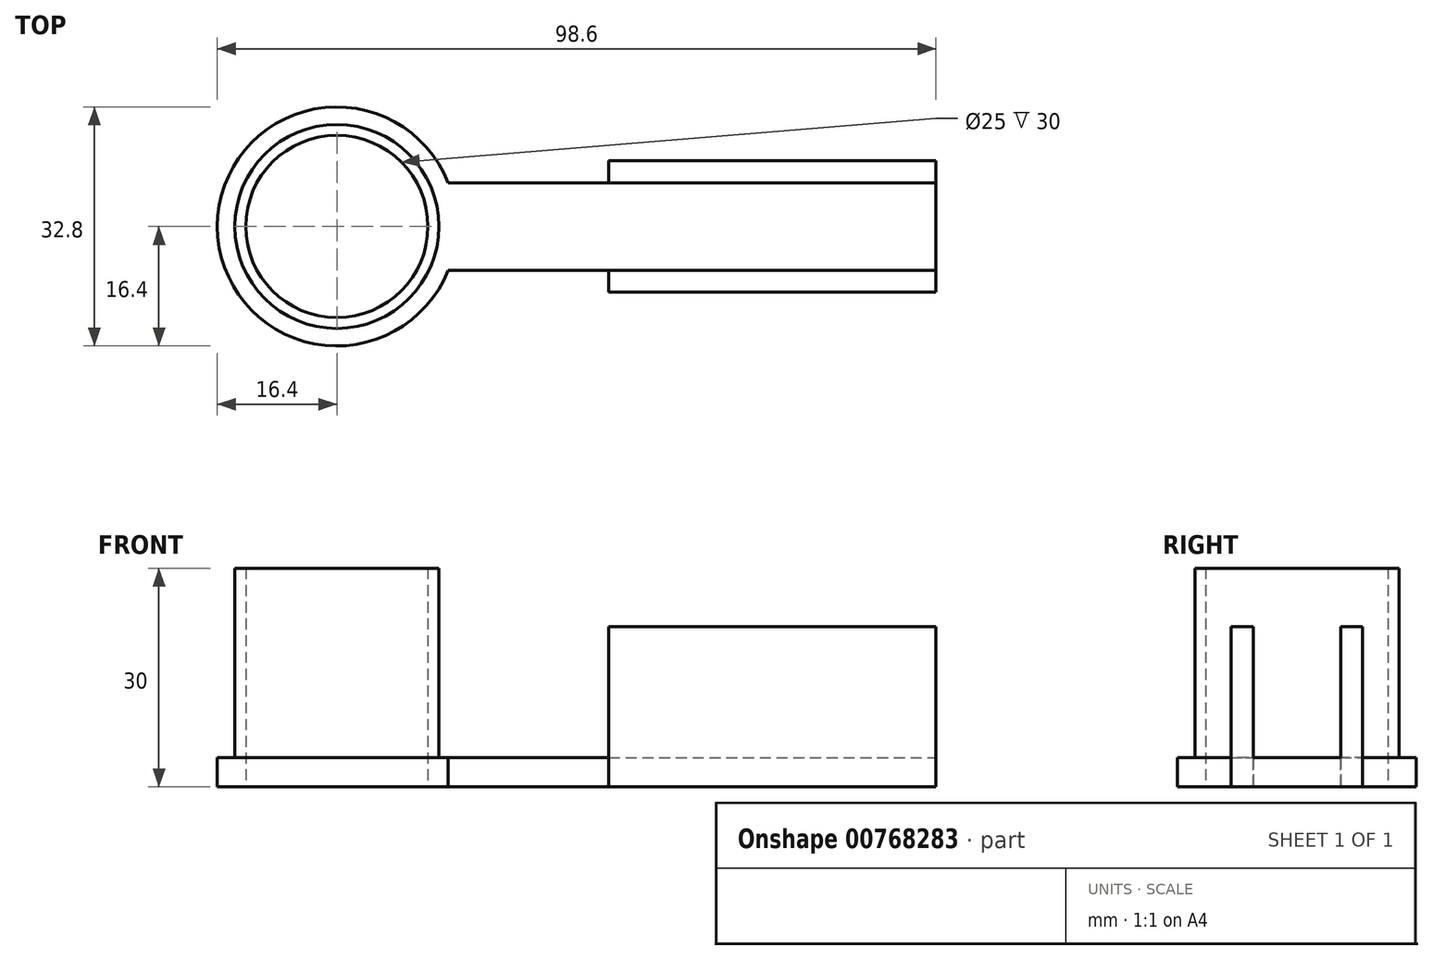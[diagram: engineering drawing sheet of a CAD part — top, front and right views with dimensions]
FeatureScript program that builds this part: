
annotation { "Feature Type Name" : "Feature", "Feature Type Description" : "" }
export const myFeature = defineFeature(function(context is Context, id is Id, definition is map)
    precondition{}
    {
        {
            var Q0;
            Q0=qCreatedBy(makeId("Top.planeOp"),FACE);
            var sketch = newSketch(context, id + "F0", { "sketchPlane" : qUnion([Q0])});
            skCircle(sketch, "E0", {"center": v(0, 0) * mm, "radius": 12.5 * mm});
            skCircle(sketch, "E1", {"center": v(0, 0) * mm, "radius": 16.4 * mm});
            skSolve(sketch);
        }
        {
            var Q0;
            Q0=qCreatedBy(makeId("Top.planeOp"),FACE);
            var sketch = newSketch(context, id + "F1", { "sketchPlane" : qUnion([Q0])});
            skCircle(sketch, "E2", {"center": v(0, 0) * mm, "radius": 12.5 * mm});
            skCircle(sketch, "E3", {"center": v(0, 0) * mm, "radius": 14 * mm});
            skSolve(sketch);
        }
        {
            var Q0;
            Q0=qCreatedBy(makeId("Top.planeOp"),FACE);
            var sketch = newSketch(context, id + "F2", { "sketchPlane" : qUnion([Q0])});
            skPoint(sketch, "E4.middle", {"position": v(-1, 0) * mm});
            skLineSegment(sketch, "E5.bottom", {"start": v(37.33, -6) * mm, "end": v(14.33, -6) * mm});
            skLineSegment(sketch, "E5.top", {"start": v(37.33, 6) * mm, "end": v(14.33, 6) * mm});
            skLineSegment(sketch, "E5.right", {"start": v(-118.08, -6) * mm, "end": v(-118.08, 6) * mm});
            skPoint(sketch, "E6", {"position": v(14.33, 6) * mm});
            skPoint(sketch, "E7", {"position": v(14.33, -6) * mm});
            skArc(sketch, "E8", {"start": v(14.33, -6) * mm, "mid": v(15.37, 0) * mm, "end": v(14.33, 6) * mm});
            skLineSegment(sketch, "E9", {"start": v(37.33, -6) * mm, "end": v(37.33, 6) * mm});
            skSolve(sketch);
        }
        {
            var Q0;
            Q0 = qSketchRegion(id + "F0", true);
            extrude(context, id + "F3", {"entities" : qUnion([Q0]), "depth" : 4 * mm, "offsetDistance" : 25 * mm});
        }
        {
            var Q0;
            Q0 = qSketchRegion(id + "F1", true);
            extrude(context, id + "F4", {"entities" : qUnion([Q0]), "operationType" : NewBodyOperationType.ADD, "depth" : 30 * mm, "offsetDistance" : 25 * mm, "hasSecondDirection" : true, "secondDirectionOppositeDirection" : false, "secondDirectionDepth" : 4 * mm});
        }
        {
            var Q0;
            Q0 = qSketchRegion(id + "F2", true);
            extrude(context, id + "F5", {"entities" : qUnion([Q0]), "operationType" : NewBodyOperationType.ADD, "depth" : 4 * mm, "offsetDistance" : 25 * mm});
        }
        {
            var Q0;
            Q0=qCreatedBy(makeId("Right.planeOp"),FACE);
            var sketch = newSketch(context, id + "F6", { "sketchPlane" : qUnion([Q0])});
            skLineSegment(sketch, "E10", {"start": v(-6, 0) * mm, "end": v(6, 0) * mm});
            skLineSegment(sketch, "E11", {"start": v(6, 0) * mm, "end": v(6, 0) * mm});
            skLineSegment(sketch, "E12", {"start": v(6, 0) * mm, "end": v(-6, 0) * mm});
            skLineSegment(sketch, "E13", {"start": v(-6, 0) * mm, "end": v(-6, 0) * mm});
            skLineSegment(sketch, "E14", {"start": v(6, 0) * mm, "end": v(9, 0) * mm});
            skLineSegment(sketch, "E15", {"start": v(9, 0) * mm, "end": v(9, 22) * mm});
            skLineSegment(sketch, "E16", {"start": v(9, 22) * mm, "end": v(6, 22) * mm});
            skLineSegment(sketch, "E17", {"start": v(6, 22) * mm, "end": v(6, 4) * mm});
            skLineSegment(sketch, "E18", {"start": v(-6, 0) * mm, "end": v(-9, 0) * mm});
            skLineSegment(sketch, "E19", {"start": v(-9, 0) * mm, "end": v(-9, 22) * mm});
            skLineSegment(sketch, "E20", {"start": v(-9, 22) * mm, "end": v(-6, 22) * mm});
            skLineSegment(sketch, "E21", {"start": v(-6, 22) * mm, "end": v(-6, 4) * mm});
            skLineSegment(sketch, "E22", {"start": v(6, 4) * mm, "end": v(-6, 4) * mm});
            skSolve(sketch);
        }
        {
            var Q0;
            Q0 = qSketchRegion(id + "F6", true);
            extrude(context, id + "F7", {"entities" : qUnion([Q0]), "operationType" : NewBodyOperationType.ADD, "depth" : 82.2 * mm, "offsetDistance" : 25 * mm, "hasSecondDirection" : true, "secondDirectionOppositeDirection" : false, "secondDirectionDepth" : 37.3 * mm});
        }
    });
